# Revit family: FU_Table_Sandler_Cono 4002 - Complete
name_source: partatom
category: Furniture
units: mm (PartAtom-declared; Revit-internal decimal feet)

## family parameters
Always vertical = No
Cut with Voids When Loaded = No
OmniClass Number = 23.21.23.15.17
Render Appearance Source = Family Geometry
Room Calculation Point = No
Shared = No
Work Plane-Based = Yes

## types (3) — shared parameters
BIMobject category = Table
BIMobject category code = furniture-table
BIMobject main category = Furniture
BIMobject main category code = furniture
Base Material = Metal - M2 Lacquer - Pearl White RAL 1013
Brand url = https://www.sandlerseating.com
Depth = 600 mm  [stored 1.9685 ft]
Edition number = 1
Height = 720 mm  [stored 2.3622 ft]
IFC Classification = Furnishing Element
Manufacturer = Sandler
Manufacturer country = USA
Manufacturer name = Sandler
Masterformat 2014 Code = 12 48 43.13
Masterformat 2014 Description = Table Mats
OmniClass Code = 23-21 23 15 17
Product Guid = ??
Product SKU = ??
Product data url = https://www.sandlerseating.com
Product family = Furniture
Product group = Table
Product name = CONO 4002
Product url = https://www.sandlerseating.com
QR code = https://www.sandlerseating.com
URL = https://www.sandlerseating.com
Uniformat II Description = Movable Furnishings
Width = 600 mm  [stored 1.9685 ft]
zero-valued in all types: Default Elevation

## per-type parameters (varying)
| type | Description | Model | Top Type |
| CONO 4002 - D36 | Dining table with wider metal base and table top measuring 90cm/36" in diameter. 75cm/29.5" high. The round table top is available in woodgrain or a lacquered finish, with a reverse knife edge profile. Other profiles and materials available by special request. | CONO 4002 D36 | FU_Top_Sandler_EF125 : 125EF Top 90dia |
| CONO 4002 - D40 | Dining table with wider metal base and table top measuring 100cm/40" in diameter. 75cm/29.5" high. The round table top is available in woodgrain or a lacquered finish, with a reverse knife edge profile. Other profiles and materials available by special request. | CONO 4002 D40 | FU_Top_Sandler_EF125 : 125EF Top 100dia |
| CONO 4002 - D48 | Dining table with wider metal base and table top measuring 120cm/48" in diameter. 75cm/29.5" high. The round table top is available in woodgrain or a lacquered finish, with a reverse knife edge profile. Other profiles and materials available by special request. | CONO 4002 D48 | FU_Top_Sandler_EF125 : 125EF Top 120dia |

note: [stored X ft] marks values corroborated as IEEE doubles in the binary element streams (Revit-internal decimal feet)

## geometry (parser evidence)
native form markers: Sweep x8
no freeform markers — native parametric forms only
